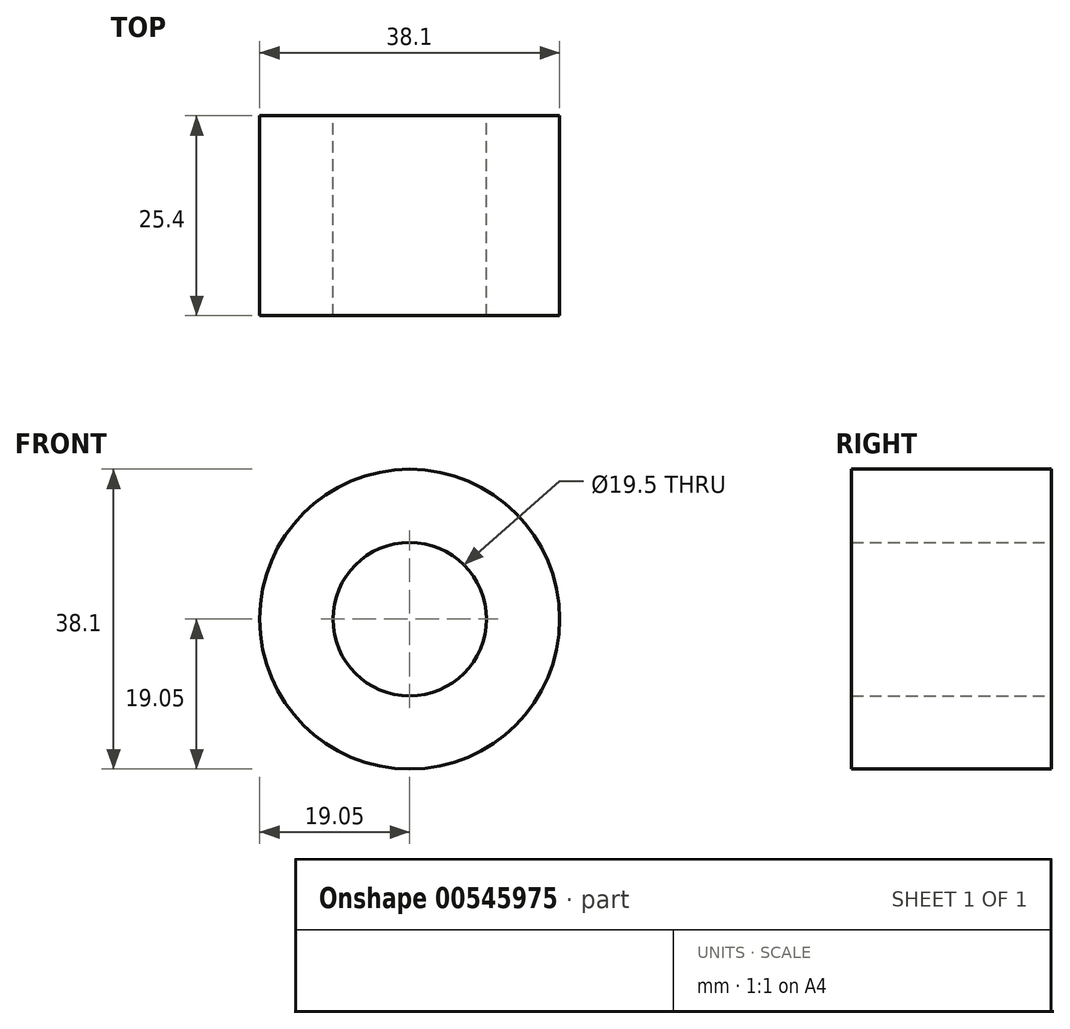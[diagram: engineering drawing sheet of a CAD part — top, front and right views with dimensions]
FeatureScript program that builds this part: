
annotation { "Feature Type Name" : "Feature", "Feature Type Description" : "" }
export const myFeature = defineFeature(function(context is Context, id is Id, definition is map)
    precondition{}
    {
        {
            var Q0;
            Q0=qCreatedBy(makeId("Front.planeOp"),FACE);
            var sketch = newSketch(context, id + "F0", { "sketchPlane" : qUnion([Q0])});
            skCircle(sketch, "E0", {"center": v(0, 0) * mm, "radius": 19.05 * mm});
            skCircle(sketch, "E1", {"center": v(0, 0) * mm, "radius": 9.75 * mm});
            skSolve(sketch);
        }
        {
            var Q0;
            Q0=makeQuery(id+"F0.imprint","IMPRINT",FACE,{"disambiguationData":[TD([[makeQuery(id+"F0.imprint","IMPRINT",EDGE,{"derivedFrom":sQuery(id+"F0.wireOp",EDGE,"E0")}),1.0]])]});
            extrude(context, id + "F1", {"entities" : qUnion([Q0]), "depth" : 25.4 * mm, "offsetDistance" : 25.4 * mm});
        }
    });
